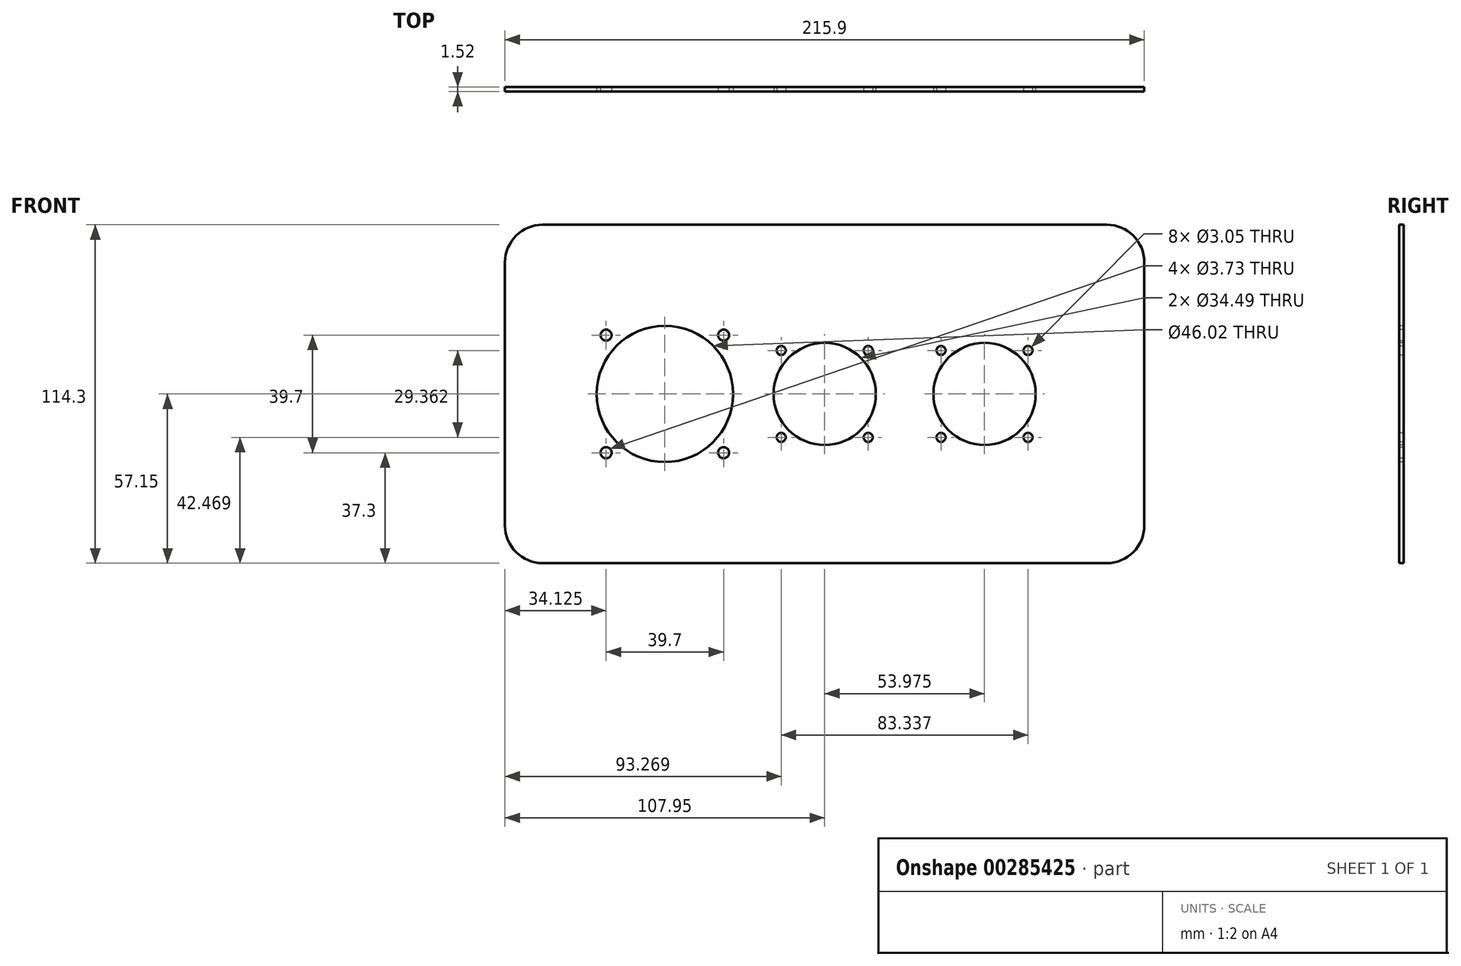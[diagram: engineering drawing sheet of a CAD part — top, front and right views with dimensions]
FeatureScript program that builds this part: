
annotation { "Feature Type Name" : "Feature", "Feature Type Description" : "" }
export const myFeature = defineFeature(function(context is Context, id is Id, definition is map)
    precondition{}
    {
        {
            var Q0;
            Q0=qCreatedBy(makeId("Front.planeOp"),FACE);
            var sketch = newSketch(context, id + "F0", { "sketchPlane" : qUnion([Q0])});
            skLineSegment(sketch, "E0.bottom", {"start": v(33.27, -22.23) * mm, "end": v(182.63, -22.23) * mm, "construction": true});
            skLineSegment(sketch, "E0.top", {"start": v(33.27, -92.08) * mm, "end": v(182.63, -92.08) * mm, "construction": true});
            skLineSegment(sketch, "E0.left", {"start": v(24.13, -31.37) * mm, "end": v(24.13, -82.93) * mm, "construction": true});
            skLineSegment(sketch, "E0.right", {"start": v(191.77, -31.37) * mm, "end": v(191.77, -82.93) * mm, "construction": true});
            skPoint(sketch, "E1.visualSharp", {"position": v(24.13, -22.23) * mm});
            skArc(sketch, "E1.filletArc", {"start": v(33.27, -22.23) * mm, "mid": v(26.8, -24.9) * mm, "end": v(24.13, -31.37) * mm, "construction": true});
            skPoint(sketch, "E2.visualSharp", {"position": v(191.77, -22.23) * mm});
            skArc(sketch, "E2.filletArc", {"start": v(191.77, -31.37) * mm, "mid": v(189.1, -24.9) * mm, "end": v(182.63, -22.22) * mm, "construction": true});
            skPoint(sketch, "E3.visualSharp", {"position": v(191.77, -92.08) * mm});
            skArc(sketch, "E3.filletArc", {"start": v(182.63, -92.08) * mm, "mid": v(189.1, -89.4) * mm, "end": v(191.77, -82.93) * mm, "construction": true});
            skPoint(sketch, "E4.visualSharp", {"position": v(24.13, -92.08) * mm});
            skArc(sketch, "E4.filletArc", {"start": v(24.13, -82.93) * mm, "mid": v(26.8, -89.4) * mm, "end": v(33.27, -92.07) * mm, "construction": true});
            skLineSegment(sketch, "E5.bottom", {"start": v(12.7, 0) * mm, "end": v(203.2, 0) * mm});
            skLineSegment(sketch, "E5.top", {"start": v(12.7, -114.3) * mm, "end": v(203.2, -114.3) * mm});
            skLineSegment(sketch, "E5.left", {"start": v(0, -12.7) * mm, "end": v(0, -101.6) * mm});
            skLineSegment(sketch, "E5.right", {"start": v(215.9, -12.7) * mm, "end": v(215.9, -101.6) * mm});
            skPoint(sketch, "E6.visualSharp", {"position": v(0, 0) * mm});
            skArc(sketch, "E6.filletArc", {"start": v(12.7, 0) * mm, "mid": v(3.72, -3.72) * mm, "end": v(0, -12.7) * mm});
            skPoint(sketch, "E7.visualSharp", {"position": v(215.9, 0) * mm});
            skArc(sketch, "E7.filletArc", {"start": v(215.9, -12.7) * mm, "mid": v(212.18, -3.72) * mm, "end": v(203.2, 0) * mm});
            skPoint(sketch, "E8.visualSharp", {"position": v(215.9, -114.3) * mm});
            skArc(sketch, "E8.filletArc", {"start": v(203.2, -114.3) * mm, "mid": v(212.18, -110.58) * mm, "end": v(215.9, -101.6) * mm});
            skPoint(sketch, "E9.visualSharp", {"position": v(0, -114.3) * mm});
            skArc(sketch, "E9.filletArc", {"start": v(0, -101.6) * mm, "mid": v(3.72, -110.58) * mm, "end": v(12.7, -114.3) * mm});
            skLineSegment(sketch, "E10", {"start": v(107.95, 0) * mm, "end": v(107.95, -114.3) * mm, "construction": true});
            skLineSegment(sketch, "E11", {"start": v(0, -57.15) * mm, "end": v(215.9, -57.15) * mm, "construction": true});
            skPoint(sketch, "E12", {"position": v(107.95, -22.23) * mm});
            skPoint(sketch, "E13", {"position": v(191.77, -57.15) * mm});
            skPoint(sketch, "E14", {"position": v(10.16, -9.52) * mm});
            skPoint(sketch, "E15", {"position": v(107.95, -9.52) * mm});
            skPoint(sketch, "E16", {"position": v(205.74, -9.52) * mm});
            skPoint(sketch, "E17", {"position": v(205.74, -104.78) * mm});
            skPoint(sketch, "E18", {"position": v(107.95, -104.78) * mm});
            skPoint(sketch, "E19", {"position": v(10.16, -104.78) * mm});
            skLineSegment(sketch, "E20", {"start": v(10.16, -9.52) * mm, "end": v(10.16, -104.78) * mm, "construction": true});
            skSolve(sketch);
        }
        {
            var Q0;
            Q0=makeQuery(id+"F0.imprint","IMPRINT",FACE,{"disambiguationData":[TD([[makeQuery(id+"F0.imprint","IMPRINT",EDGE,{"derivedFrom":sQuery(id+"F0.wireOp",EDGE,"E5.bottom")}),-1.0]])]});
            extrude(context, id + "F1", {"entities" : qUnion([Q0]), "depth" : 1.52 * mm});
        }
        {
            var Q0;
            Q0=makeQuery(id+"F1.opExtrude","CAP_FACE",FACE,{"disambiguationData":[OSD([sQuery(id+"F0.wireOp",EDGE,"E5.bottom"),sQuery(id+"F0.wireOp",EDGE,"E5.top"),sQuery(id+"F0.wireOp",EDGE,"E5.left"),sQuery(id+"F0.wireOp",EDGE,"E5.right"),sQuery(id+"F0.wireOp",EDGE,"E6.filletArc"),sQuery(id+"F0.wireOp",EDGE,"E7.filletArc"),sQuery(id+"F0.wireOp",EDGE,"E8.filletArc"),sQuery(id+"F0.wireOp",EDGE,"E9.filletArc")])],"isStart":false});
            var sketch = newSketch(context, id + "F2", { "sketchPlane" : qUnion([Q0])});
            skCircle(sketch, "E21", {"center": v(53.97, -57.15) * mm, "radius": 23.01 * mm});
            skCircle(sketch, "E22", {"center": v(34.12, -37.3) * mm, "radius": 1.87 * mm});
            skLineSegment(sketch, "E23.bottom", {"start": v(34.12, -37.3) * mm, "end": v(73.83, -37.3) * mm, "construction": true});
            skLineSegment(sketch, "E23.top", {"start": v(34.12, -77) * mm, "end": v(73.83, -77) * mm, "construction": true});
            skLineSegment(sketch, "E23.left", {"start": v(34.12, -37.3) * mm, "end": v(34.12, -77) * mm, "construction": true});
            skLineSegment(sketch, "E23.right", {"start": v(73.83, -37.3) * mm, "end": v(73.83, -77) * mm, "construction": true});
            skLineSegment(sketch, "E24", {"start": v(53.98, -37.3) * mm, "end": v(53.98, -77) * mm, "construction": true});
            skLineSegment(sketch, "E25", {"start": v(34.12, -57.15) * mm, "end": v(73.83, -57.15) * mm, "construction": true});
            skCircle(sketch, "E26", {"center": v(73.83, -37.3) * mm, "radius": 1.87 * mm});
            skCircle(sketch, "E27", {"center": v(73.83, -77) * mm, "radius": 1.87 * mm});
            skCircle(sketch, "E28", {"center": v(34.12, -77) * mm, "radius": 1.87 * mm});
            skCircle(sketch, "E29", {"center": v(161.93, -57.15) * mm, "radius": 17.25 * mm});
            skCircle(sketch, "E30", {"center": v(147.24, -42.47) * mm, "radius": 1.52 * mm});
            skLineSegment(sketch, "E31.bottom", {"start": v(147.24, -42.47) * mm, "end": v(176.6, -42.47) * mm, "construction": true});
            skLineSegment(sketch, "E31.top", {"start": v(147.24, -71.83) * mm, "end": v(176.6, -71.83) * mm, "construction": true});
            skLineSegment(sketch, "E31.left", {"start": v(147.24, -42.47) * mm, "end": v(147.24, -71.83) * mm, "construction": true});
            skLineSegment(sketch, "E31.right", {"start": v(176.6, -42.47) * mm, "end": v(176.6, -71.83) * mm, "construction": true});
            skLineSegment(sketch, "E32", {"start": v(161.93, -42.47) * mm, "end": v(161.93, -71.83) * mm, "construction": true});
            skLineSegment(sketch, "E33", {"start": v(147.24, -57.15) * mm, "end": v(176.6, -57.15) * mm, "construction": true});
            skCircle(sketch, "E34", {"center": v(176.6, -42.47) * mm, "radius": 1.52 * mm});
            skCircle(sketch, "E35", {"center": v(176.6, -71.83) * mm, "radius": 1.52 * mm});
            skCircle(sketch, "E36", {"center": v(147.24, -71.83) * mm, "radius": 1.52 * mm});
            skCircle(sketch, "E37", {"center": v(107.95, -57.15) * mm, "radius": 17.25 * mm});
            skLineSegment(sketch, "E38.bottom", {"start": v(93.27, -42.47) * mm, "end": v(122.63, -42.47) * mm, "construction": true});
            skLineSegment(sketch, "E38.top", {"start": v(93.27, -71.83) * mm, "end": v(122.63, -71.83) * mm, "construction": true});
            skLineSegment(sketch, "E38.left", {"start": v(93.27, -42.47) * mm, "end": v(93.27, -71.83) * mm, "construction": true});
            skLineSegment(sketch, "E38.right", {"start": v(122.63, -42.47) * mm, "end": v(122.63, -71.83) * mm, "construction": true});
            skLineSegment(sketch, "E39", {"start": v(122.63, -57.15) * mm, "end": v(93.27, -57.15) * mm, "construction": true});
            skLineSegment(sketch, "E40", {"start": v(107.95, -71.83) * mm, "end": v(107.95, -42.47) * mm, "construction": true});
            skCircle(sketch, "E41", {"center": v(93.27, -42.47) * mm, "radius": 1.52 * mm});
            skCircle(sketch, "E42", {"center": v(122.63, -42.47) * mm, "radius": 1.52 * mm});
            skCircle(sketch, "E43", {"center": v(122.63, -71.83) * mm, "radius": 1.52 * mm});
            skCircle(sketch, "E44", {"center": v(93.27, -71.83) * mm, "radius": 1.52 * mm});
            skSolve(sketch);
        }
        {
            var Q0;
            Q0=qSketchRegion(id+"F2",true);
            extrude(context, id + "F3", {"entities" : qUnion([Q0]), "operationType" : NewBodyOperationType.REMOVE, "endBound" : BoundingType.THROUGH_ALL, "oppositeDirection" : true, "depth" : 25.4 * mm});
        }
    });
